# Revit family: Drain_Deck_Parking_Heavy-Duty-Zurn-Z536-With-Support-Flange
name_source: partatom
category: Plumbing Fixtures
units: mm (PartAtom-declared; Revit-internal decimal feet)

## family parameters
Always vertical = Yes
Cut with Voids When Loaded = No
Maintain Annotation Orientation = No
OmniClass Number = 23.70.50.21.24.14
OmniClass Title = Deck Waste Water Drains
Part Type = Normal
Room Calculation Point = No
Round Connector Dimension = Use Radius
Shared = No
Work Plane-Based = No

## types (14) — shared parameters
Assembly Code = D2030300
CW Connection = No
Default Elevation = 25 "
Description = 15-3/8 [391] DIAMETER HEAVY-DUTY PARKING DECK DRAIN WITH SUPPORT FLANGE
Grate Open Area Sq.in = 56 "
HW Connection = No
Main Material = Iron - Zurn - Cast - Painted - Blue
Manufacturer = Zurn Water, LLC
Manufacurer Brand = Zurn
Modified Date = 12/26/2025
Product Documentation Link = https://files.zurn.com
Product Installtion Sheet = https://files.zurn.com
Product Page URL = https://www.zurn.com
Product data url = https://www.bimobject.com
Top Diameter Inner = 15.375 "
Top Diameter Width = 20 "
URL = www.zurn.com
Vent Connection = No
WFU = 1
Waste Connection = Yes
zero-valued in all types: CWFU, HWFU

## per-type parameters (varying)
| type | A_ Pipe Size (Actual-Inner) | A_ Pipe Size (Actual-Outer) | A_ Pipe Size (Nominal) | Approx. Weight (Lbs) | Body Height_E | Connector Radius | Frame Dimension | Grate | Model | Type Comments | ZN-Top |
| Z536-3NH | 3.068 " | 3.5 " | 3 " | 95 " | 5.25 " | 1.5 " | 2 " | Iron - Zurn - Cast - Painted - Blue | Z536 | Z536-3 Inch-No-Hub Outlet | No |
| Z536-3NL | 3.068 " | 3.5 " | 3 " | 95 " | 4.625 " | 1.5 " | 2 " | Iron - Zurn - Cast - Painted - Blue | Z536 | Z536-3 Inch-Neo-Loc Outlet | No |
| Z536-4IP | 4.026 " | 4.5 " | 4 " | 95 " | 3.75 " | 2 " | 2 " | Iron - Zurn - Cast - Painted - Blue | Z536 | Z536-4 Inch-Threaded Outlet | No |
| Z536-4NH | 4.026 " | 4.5 " | 4 " | 95 " | 5.25 " | 2 " | 2 " | Iron - Zurn - Cast - Painted - Blue | Z536 | Z536-4 Inch-No-Hub Outlet | No |
| Z536-4NL | 4.026 " | 4.5 " | 4 " | 95 " | 4.625 " | 2 " | 2 " | Iron - Zurn - Cast - Painted - Blue | Z536 | Z536-4 Inch-Neo-Loc Outlet | No |
| Z536-6NH | 6.065 " | 6.625 " | 6 " | 95 " | 5.25 " | 3 " | 2 " | Iron - Zurn - Cast - Painted - Blue | Z536 | Z536-6 Inch-No-Hub Outlet | No |
| Z536-8NH | 7.981 " | 8.625 " | 8 " | 97 " | 5.25 " | 4 " | 2 " | Iron - Zurn - Cast - Painted - Blue | Z536 | Z536-8 Inch-No-Hub Outlet | No |
| ZN536-3NH | 3.068 " | 3.5 " | 3 " | 95 " | 5.25 " | 1.5 " | 2.188 " | Bronze - Zurn - Polished Nickel | ZN536 | ZN536-3 Inch-No-Hub Outlet | Yes |
| ZN536-3NL | 3.068 " | 3.5 " | 3 " | 95 " | 4.625 " | 1.5 " | 2.188 " | Bronze - Zurn - Polished Nickel | ZN536 | ZN536-3 Inch-Neo-Loc Outlet | Yes |
| ZN536-4IP | 4.026 " | 4.5 " | 4 " | 95 " | 3.75 " | 2 " | 2.188 " | Bronze - Zurn - Polished Nickel | ZN536 | ZN536-4 Inch-Threaded Outlet | Yes |
| ZN536-4NH | 4.026 " | 4.5 " | 4 " | 95 " | 5.25 " | 2 " | 2.188 " | Bronze - Zurn - Polished Nickel | ZN536 | ZN536-4 Inch-No-Hub Outlet | Yes |
| ZN536-4NL | 4.026 " | 4.5 " | 4 " | 95 " | 4.625 " | 2 " | 2.188 " | Bronze - Zurn - Polished Nickel | ZN536 | ZN536-4 Inch-Neo-Loc Outlet | Yes |
| ZN536-6NH | 6.065 " | 6.625 " | 6 " | 95 " | 5.25 " | 3 " | 2.188 " | Bronze - Zurn - Polished Nickel | ZN536 | ZN536-6 Inch-No-Hub Outlet | Yes |
| ZN536-8NH | 7.981 " | 8.625 " | 8 " | 97 " | 5.25 " | 4 " | 2.188 " | Bronze - Zurn - Polished Nickel | ZN536 | ZN536-8 Inch-No-Hub Outlet | Yes |

## geometry (parser evidence)
native form markers: Sweep x5
no freeform markers — native parametric forms only
